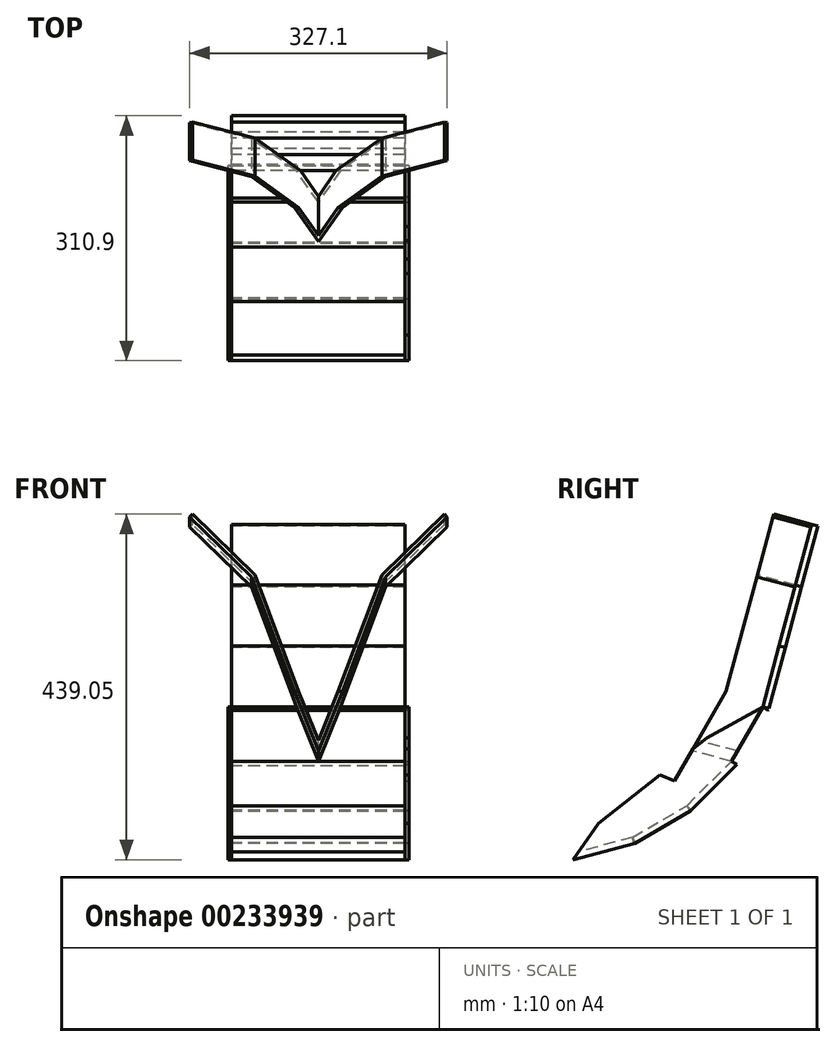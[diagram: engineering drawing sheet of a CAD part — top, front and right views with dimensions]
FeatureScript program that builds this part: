
annotation { "Feature Type Name" : "Feature", "Feature Type Description" : "" }
export const myFeature = defineFeature(function(context is Context, id is Id, definition is map)
    precondition{}
    {
        {
            assignVariable(context, id + "F0", {"variableType" : VariableType.LENGTH, "name" : "CutWidth", "lengthValue" : 220 * mm});
        }
        {
            var Q0;
            Q0=qCreatedBy(makeId("Right.planeOp"),FACE);
            var sketch = newSketch(context, id + "F1", { "sketchPlane" : qUnion([Q0])});
            skLineSegment(sketch, "E0", {"start": v(0, 0) * mm, "end": v(77.27, 20.7) * mm});
            skLineSegment(sketch, "E1", {"start": v(77.27, 20.7) * mm, "end": v(75.2, 28.43) * mm});
            skLineSegment(sketch, "E2", {"start": v(75.2, 28.43) * mm, "end": v(7.14, 10.2) * mm});
            skLineSegment(sketch, "E3", {"start": v(7.14, 10.2) * mm, "end": v(0, 0) * mm});
            skSolve(sketch);
        }
        {
            var Q0;
            Q0 = qSketchRegion(id + "F1", true);
            extrude(context, id + "F2", {"entities" : qUnion([Q0]), "endBound" : BoundingType.SYMMETRIC, "depth" : getVariable(context, 'CutWidth'), "offsetDistance" : 25 * mm});
        }
        {
            var Q0;
            Q0=qCreatedBy(makeId("Right.planeOp"),FACE);
            var sketch = newSketch(context, id + "F3", { "sketchPlane" : qUnion([Q0])});
            skLineSegment(sketch, "E4", {"start": v(75.2, 28.43) * mm, "end": v(144.49, 68.43) * mm});
            skLineSegment(sketch, "E5", {"start": v(144.49, 68.43) * mm, "end": v(148.49, 61.5) * mm});
            skLineSegment(sketch, "E6", {"start": v(148.49, 61.5) * mm, "end": v(79.2, 21.5) * mm});
            skLineSegment(sketch, "E7", {"start": v(79.2, 21.5) * mm, "end": v(75.2, 28.43) * mm});
            skSolve(sketch);
        }
        {
            var Q0;
            Q0 = qSketchRegion(id + "F3", true);
            extrude(context, id + "F4", {"entities" : qUnion([Q0]), "endBound" : BoundingType.SYMMETRIC, "depth" : getVariable(context, 'CutWidth'), "offsetDistance" : 25 * mm});
        }
        {
            var Q0;
            Q0=qCreatedBy(makeId("Right.planeOp"),FACE);
            var sketch = newSketch(context, id + "F5", { "sketchPlane" : qUnion([Q0])});
            skLineSegment(sketch, "E8", {"start": v(144.49, 68.43) * mm, "end": v(201.05, 125) * mm});
            skLineSegment(sketch, "E9", {"start": v(201.05, 125) * mm, "end": v(206.71, 119.34) * mm});
            skLineSegment(sketch, "E10", {"start": v(206.71, 119.34) * mm, "end": v(150.14, 62.78) * mm});
            skLineSegment(sketch, "E11", {"start": v(150.14, 62.78) * mm, "end": v(144.49, 68.43) * mm});
            skSolve(sketch);
        }
        {
            var Q0;
            Q0 = qSketchRegion(id + "F5", true);
            extrude(context, id + "F6", {"entities" : qUnion([Q0]), "endBound" : BoundingType.SYMMETRIC, "depth" : getVariable(context, 'CutWidth'), "offsetDistance" : 25 * mm});
        }
        {
            var Q0;
            Q0=qCreatedBy(makeId("Right.planeOp"),FACE);
            var sketch = newSketch(context, id + "F7", { "sketchPlane" : qUnion([Q0])});
            skLineSegment(sketch, "E12", {"start": v(201.05, 125) * mm, "end": v(241.05, 194.28) * mm});
            skLineSegment(sketch, "E13", {"start": v(241.05, 194.28) * mm, "end": v(247.98, 190.28) * mm});
            skLineSegment(sketch, "E14", {"start": v(247.98, 190.28) * mm, "end": v(207.98, 121) * mm});
            skLineSegment(sketch, "E15", {"start": v(207.98, 121) * mm, "end": v(201.05, 125) * mm});
            skSolve(sketch);
        }
        {
            var Q0;
            Q0 = qSketchRegion(id + "F7", true);
            extrude(context, id + "F8", {"entities" : qUnion([Q0]), "endBound" : BoundingType.SYMMETRIC, "depth" : getVariable(context, 'CutWidth'), "offsetDistance" : 25 * mm});
        }
        {
            var Q0;
            Q0=qCreatedBy(makeId("Right.planeOp"),FACE);
            var sketch = newSketch(context, id + "F9", { "sketchPlane" : qUnion([Q0])});
            skLineSegment(sketch, "E16", {"start": v(241.05, 194.28) * mm, "end": v(261.76, 271.56) * mm});
            skLineSegment(sketch, "E17", {"start": v(261.76, 271.56) * mm, "end": v(269.49, 269.49) * mm});
            skLineSegment(sketch, "E18", {"start": v(269.49, 269.49) * mm, "end": v(248.78, 192.21) * mm});
            skLineSegment(sketch, "E19", {"start": v(248.78, 192.21) * mm, "end": v(241.05, 194.28) * mm});
            skSolve(sketch);
        }
        {
            var Q0;
            Q0 = qSketchRegion(id + "F9", true);
            extrude(context, id + "F10", {"entities" : qUnion([Q0]), "endBound" : BoundingType.SYMMETRIC, "depth" : getVariable(context, 'CutWidth'), "offsetDistance" : 25 * mm});
        }
        {
            var Q0;
            Q0=qCreatedBy(makeId("Right.planeOp"),FACE);
            var sketch = newSketch(context, id + "F11", { "sketchPlane" : qUnion([Q0])});
            skLineSegment(sketch, "E20", {"start": v(261.76, 271.56) * mm, "end": v(282.47, 348.83) * mm});
            skLineSegment(sketch, "E21", {"start": v(282.47, 348.83) * mm, "end": v(290.2, 346.76) * mm});
            skLineSegment(sketch, "E22", {"start": v(290.2, 346.76) * mm, "end": v(269.49, 269.49) * mm});
            skLineSegment(sketch, "E23", {"start": v(269.49, 269.49) * mm, "end": v(261.76, 271.56) * mm});
            skSolve(sketch);
        }
        {
            var Q0;
            Q0 = qSketchRegion(id + "F11", true);
            extrude(context, id + "F12", {"entities" : qUnion([Q0]), "endBound" : BoundingType.SYMMETRIC, "depth" : getVariable(context, 'CutWidth'), "offsetDistance" : 25 * mm});
        }
        {
            var Q0;
            Q0=makeQuery(id+"F2.opExtrude","CAP_FACE",FACE,{"disambiguationData":[OSD([sQuery(id+"F1.wireOp",EDGE,"E0"),sQuery(id+"F1.wireOp",EDGE,"E1"),sQuery(id+"F1.wireOp",EDGE,"E2"),sQuery(id+"F1.wireOp",EDGE,"E3")])],"isStart":false});
            var sketch = newSketch(context, id + "F13", { "sketchPlane" : qUnion([Q0])});
            skLineSegment(sketch, "E24", {"start": v(0, 0) * mm, "end": v(78.3, 20.98) * mm});
            skLineSegment(sketch, "E25", {"start": v(78.3, 20.98) * mm, "end": v(149.4, 62.03) * mm});
            skLineSegment(sketch, "E26", {"start": v(149.4, 62.03) * mm, "end": v(207.46, 120.09) * mm});
            skLineSegment(sketch, "E27", {"start": v(207.46, 120.09) * mm, "end": v(247.98, 190.28) * mm});
            skLineSegment(sketch, "E28", {"start": v(247.98, 190.28) * mm, "end": v(241.05, 194.28) * mm});
            skLineSegment(sketch, "E29", {"start": v(32.16, 45.93) * mm, "end": v(0, 0) * mm});
            skLineSegment(sketch, "E30", {"start": v(241.05, 194.28) * mm, "end": v(170.21, 154.9) * mm});
            skLineSegment(sketch, "E31", {"start": v(170.21, 154.9) * mm, "end": v(32.16, 45.93) * mm});
            skSolve(sketch);
        }
        {
            var Q0;
            Q0 = qSketchRegion(id + "F13", true);
            extrude(context, id + "F14", {"entities" : qUnion([Q0]), "depth" : 5 * mm, "offsetDistance" : 25 * mm});
        }
        {
            var Q0;
            Q0=makeQuery(id+"F14.opExtrude","SWEPT_BODY",BODY,{"disambiguationData":[OSD([sQuery(id+"F13.wireOp",EDGE,"E24"),sQuery(id+"F13.wireOp",EDGE,"E25"),sQuery(id+"F13.wireOp",EDGE,"E26"),sQuery(id+"F13.wireOp",EDGE,"E27"),sQuery(id+"F13.wireOp",EDGE,"E28"),sQuery(id+"F13.wireOp",EDGE,"D1kayod4-U7Fd-qF1a-zwhq-SdJl2y3vNeEH"),sQuery(id+"F13.wireOp",EDGE,"6MnJEwqO-oXBS-JiDY-IIq7-GgJlHQkKD3KX"),sQuery(id+"F13.wireOp",EDGE,"c5WRHA9G-oh9G-S0jL-QoA0-L1UWFJedJsJK"),sQuery(id+"F13.wireOp",EDGE,"E29"),sQuery(id+"F13.wireOp",EDGE,"E30")])]});
            var Q1;
            Q1=qCreatedBy(makeId("Right.planeOp"),FACE);
            mirror(context, id + "F15", {"entities" : qUnion([Q0]), "mirrorPlane" : qUnion([Q1])});
        }
        {
            var Q0;
            Q0=qCreatedBy(makeId("Right.planeOp"),FACE);
            var sketch = newSketch(context, id + "F16", { "sketchPlane" : qUnion([Q0])});
            skLineSegment(sketch, "E32", {"start": v(282.47, 348.83) * mm, "end": v(303.17, 426.1) * mm});
            skLineSegment(sketch, "E33", {"start": v(303.17, 426.1) * mm, "end": v(310.9, 424.04) * mm});
            skLineSegment(sketch, "E34", {"start": v(310.9, 424.04) * mm, "end": v(290.2, 346.76) * mm});
            skLineSegment(sketch, "E35", {"start": v(290.2, 346.76) * mm, "end": v(282.47, 348.83) * mm});
            skSolve(sketch);
        }
        {
            var Q0;
            Q0 = qSketchRegion(id + "F16", true);
            extrude(context, id + "F17", {"entities" : qUnion([Q0]), "endBound" : BoundingType.SYMMETRIC, "depth" : getVariable(context, 'CutWidth'), "offsetDistance" : 25 * mm});
        }
        {
            var Q0;
            Q0=makeQuery(id+"F10.opExtrude","SWEPT_FACE",FACE,{"disambiguationData":[OSD([sQuery(id+"F9.wireOp",EDGE,"E16")])]});
            cPlane(context, id + "F18", {"entities" : qUnion([Q0]), "cplaneType" : CPlaneType.OFFSET, "offset" : 119 * mm, "width" : 150 * mm, "height" : 150 * mm});
        }
        {
            var Q0;
            Q0=qCreatedBy(id+"F18.planeOp",FACE);
            var sketch = newSketch(context, id + "F19", { "sketchPlane" : qUnion([Q0])});
            skLineSegment(sketch, "E36", {"start": v(-85, 407.31) * mm, "end": v(0, 172.78) * mm});
            skLineSegment(sketch, "E37", {"start": v(0, 172.78) * mm, "end": v(85, 407.31) * mm});
            skLineSegment(sketch, "E38", {"start": v(80.67, 410.05) * mm, "end": v(0, 187.45) * mm});
            skLineSegment(sketch, "E39", {"start": v(0, 187.45) * mm, "end": v(-80.67, 410.05) * mm});
            skLineSegment(sketch, "E40", {"start": v(0, 490.05) * mm, "end": v(0, 409.06) * mm, "construction": true});
            skLineSegment(sketch, "E41", {"start": v(-85, 407.31) * mm, "end": v(-163.55, 486.53) * mm});
            skLineSegment(sketch, "E42", {"start": v(-163.55, 486.53) * mm, "end": v(-160, 490.05) * mm});
            skLineSegment(sketch, "E43", {"start": v(-160, 490.05) * mm, "end": v(-80.67, 410.05) * mm});
            skLineSegment(sketch, "E44", {"start": v(80.67, 410.05) * mm, "end": v(160, 490.05) * mm});
            skLineSegment(sketch, "E45", {"start": v(160, 490.05) * mm, "end": v(163.55, 486.53) * mm});
            skLineSegment(sketch, "E46", {"start": v(163.55, 486.53) * mm, "end": v(85, 407.31) * mm});
            skSolve(sketch);
        }
        {
            var Q0;
            Q0 = qSketchRegion(id + "F19", true);
            var Q1;
            Q1=makeQuery(id+"F10.opExtrude","SWEPT_FACE",FACE,{"disambiguationData":[OSD([sQuery(id+"F9.wireOp",EDGE,"E16")])]});
            extrude(context, id + "F20", {"entities" : qUnion([Q0]), "endBound" : BoundingType.UP_TO_SURFACE, "oppositeDirection" : true, "depth" : 25 * mm, "endBoundEntityFace" : qUnion([Q1]), "offsetDistance" : 25 * mm});
        }
        {
            var Q0;
            Q0=makeQuery(id+"F10.opExtrude","CAP_FACE",FACE,{"disambiguationData":[OSD([sQuery(id+"F9.wireOp",EDGE,"E16"),sQuery(id+"F9.wireOp",EDGE,"E17"),sQuery(id+"F9.wireOp",EDGE,"E18"),sQuery(id+"F9.wireOp",EDGE,"E19")])],"isStart":false});
            var sketch = newSketch(context, id + "F21", { "sketchPlane" : qUnion([Q0])});
            skLineSegment(sketch, "E47", {"start": v(241.05, 194.28) * mm, "end": v(201.05, 125) * mm});
            skLineSegment(sketch, "E48", {"start": v(201.05, 125) * mm, "end": v(274.68, 80.52) * mm});
            skLineSegment(sketch, "E49", {"start": v(274.68, 80.52) * mm, "end": v(369.9, 104.3) * mm});
            skLineSegment(sketch, "E50", {"start": v(369.9, 104.3) * mm, "end": v(241.05, 194.28) * mm});
            skLineSegment(sketch, "E51", {"start": v(260.75, 460.97) * mm, "end": v(194.46, 213.58) * mm});
            skLineSegment(sketch, "E52", {"start": v(194.46, 213.58) * mm, "end": v(129, 100.2) * mm});
            skLineSegment(sketch, "E53", {"start": v(129, 100.2) * mm, "end": v(18.2, 145.24) * mm});
            skLineSegment(sketch, "E54", {"start": v(18.2, 145.24) * mm, "end": v(140.77, 543.36) * mm});
            skLineSegment(sketch, "E55", {"start": v(140.77, 543.36) * mm, "end": v(260.75, 460.97) * mm});
            skSolve(sketch);
        }
        {
            var Q0;
            Q0 = qSketchRegion(id + "F21", true);
            extrude(context, id + "F22", {"entities" : qUnion([Q0]), "operationType" : NewBodyOperationType.REMOVE, "endBound" : BoundingType.THROUGH_ALL, "oppositeDirection" : true, "depth" : 25 * mm, "offsetDistance" : 25 * mm, "hasSecondDirection" : true, "secondDirectionBound" : SecondDirectionBoundingType.THROUGH_ALL, "secondDirectionOppositeDirection" : false, "secondDirectionDepth" : 25 * mm});
        }
    });
